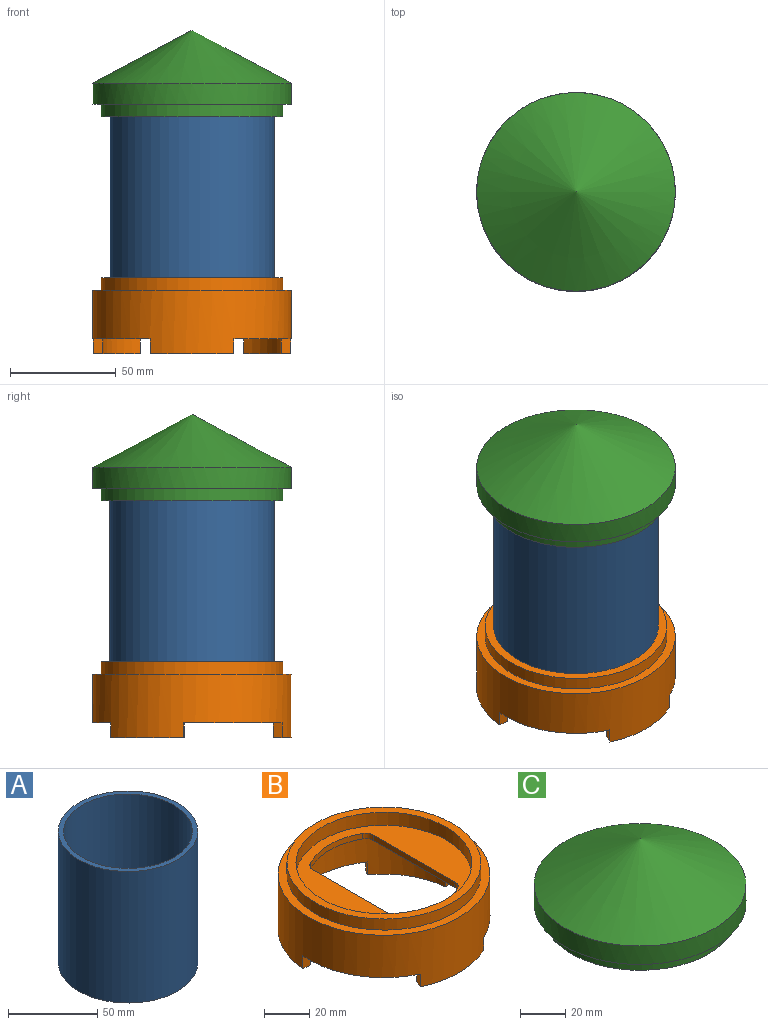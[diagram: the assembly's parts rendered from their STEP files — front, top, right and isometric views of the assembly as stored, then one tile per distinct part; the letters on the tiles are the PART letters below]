
ASSEMBLY  parts=3 mates=3
PART A: 4 faces, bbox 78x78x90 mm
  f0: cylinder r=36mm len=90mm, axis (0,0,-1), area 20357.5mm2, adj f2,f3
  f1: cylinder r=39mm len=90mm, axis (0,0,-1), area 22054mm2, adj f2,f3
  f2: plane 78x78mm, normal (0,0,1), area 706.9mm2, adj f0,f1
  f3: plane 78x78mm, normal (0,0,-1), area 706.9mm2, adj f0,f1
PART B: 28 faces, bbox 94x94x36 mm
  f0: plane 46.69x29.04mm, normal (0,0,-1), area 246mm2, adj f2,f9,f20,f25
  f1: plane 53.92x12.19mm, normal (0,0,-1), area 246mm2, adj f2,f9,f22,f26
  f2: cylinder r=47mm len=94mm, axis (0,0,-1), area 7653.4mm2, adj f0,f1,f3,f4,f19,f20,f21,f22
  f3: plane 46.69x29.04mm, normal (0,0,-1), area 246mm2, adj f2,f9,f19,f23
  f4: plane 94x94mm, normal (0,0,1), area 1131mm2, adj f2,f5
  f5: cylinder r=43mm len=86mm, axis (0,0,1), area 1621.1mm2, adj f4,f6
  f6: plane 86x86mm, normal (0,0,1), area 1030.4mm2, adj f5,f8
  f7: plane 78x78mm, normal (0,0,1), area 2341.2mm2, adj f8,f11,f12,f13,f14,f15,f16,f17
  f8: cylinder r=39mm len=78mm, axis (0,0,1), area 1715.3mm2, adj f6,f7
  f9: cylinder r=42.5mm len=85mm, axis (0,0,-1), area 5852.5mm2, adj f0,f1,f3,f10,f19,f20,f21,f22
  f10: plane 85x85mm, normal (0,0,-1), area 3237.3mm2, adj f9,f11,f12,f13,f14,f15,f16,f17
  f11: cylinder r=5mm len=4.38mm, axis (0,0,1), area 16mm2, adj f7,f10,f12,f18
  f12: cylinder r=34mm len=32.83mm, axis (0,0,1), area 102.8mm2, adj f7,f10,f11,f13
  f13: cylinder r=5mm len=4.38mm, axis (0,0,1), area 16mm2, adj f7,f10,f12,f14
  f14: plane 50.79x3mm, normal (1,0,0), area 152.4mm2, adj f7,f10,f13,f15
  f15: cylinder r=5mm len=4.38mm, axis (0,0,1), area 16mm2, adj f7,f10,f14,f16
  f16: cylinder r=34mm len=32.83mm, axis (0,0,1), area 102.8mm2, adj f7,f10,f15,f17
  f17: cylinder r=5mm len=4.38mm, axis (0,0,1), area 16mm2, adj f7,f10,f16,f18
  f18: plane 50.79x3mm, normal (-1,0,0), area 152.4mm2, adj f7,f10,f11,f17
  f19: plane 7x4.08mm, normal (0.91,0.42,0), area 31.5mm2, adj f2,f3,f9,f21
  f20: plane 7x4.08mm, normal (-0.91,0.42,0), area 31.5mm2, adj f0,f2,f9,f21
  f21: plane 39.73x8.48mm, normal (0,0,-1), area 175.7mm2, adj f2,f9,f19,f20
  f22: plane 7x3.69mm, normal (-0.82,0.57,0), area 31.5mm2, adj f1,f2,f9,f24
  f23: plane 7x4.48mm, normal (0.09,-1,0), area 31.5mm2, adj f2,f3,f9,f24
  f24: plane 34.8x22.44mm, normal (0,0,-1), area 175.7mm2, adj f2,f9,f22,f23
  f25: plane 7x4.48mm, normal (-0.09,-1,0), area 31.5mm2, adj f0,f2,f9,f27
  f26: plane 7x3.69mm, normal (0.82,0.57,0), area 31.5mm2, adj f1,f2,f9,f27
  f27: plane 34.8x22.44mm, normal (0,0,-1), area 175.7mm2, adj f2,f9,f25,f26
PART C: 7 faces, bbox 94x94x41 mm
  f0: cylinder r=47mm len=94mm, axis (0,0,-1), area 2953.1mm2, adj f4,f6
  f1: plane 86x86mm, normal (0,0,-1), area 1030.4mm2, adj f2,f3
  f2: cylinder r=39mm len=78mm, axis (0,0,-1), area 3920.7mm2, adj f1,f5
  f3: cylinder r=43mm len=86mm, axis (0,0,-1), area 1621.1mm2, adj f1,f4
  f4: plane 94x94mm, normal (0,0,-1), area 1131mm2, adj f0,f3
  f5: cone r=39mm half-angle=62deg, axis (0,0,-1), area 5412.3mm2, adj f2
  f6: cone r=0mm half-angle=62deg, axis (0,0,-1), area 7860.5mm2, adj f0
PLACE A t=(0,0,22)mm
PLACE B at identity fixed
PLACE C t=(0,0,105)mm
MATE fastened B.f2 <-> A.f0  axis (0,0,1) through (0,0,22)mm
MATE slider A.f0 <-> C.f0  axis (0,0,-1) through (0,0,67)mm
MATE slider B.f2 <-> A.f0  axis (0,0,1) through (0,0,25.5)mm
